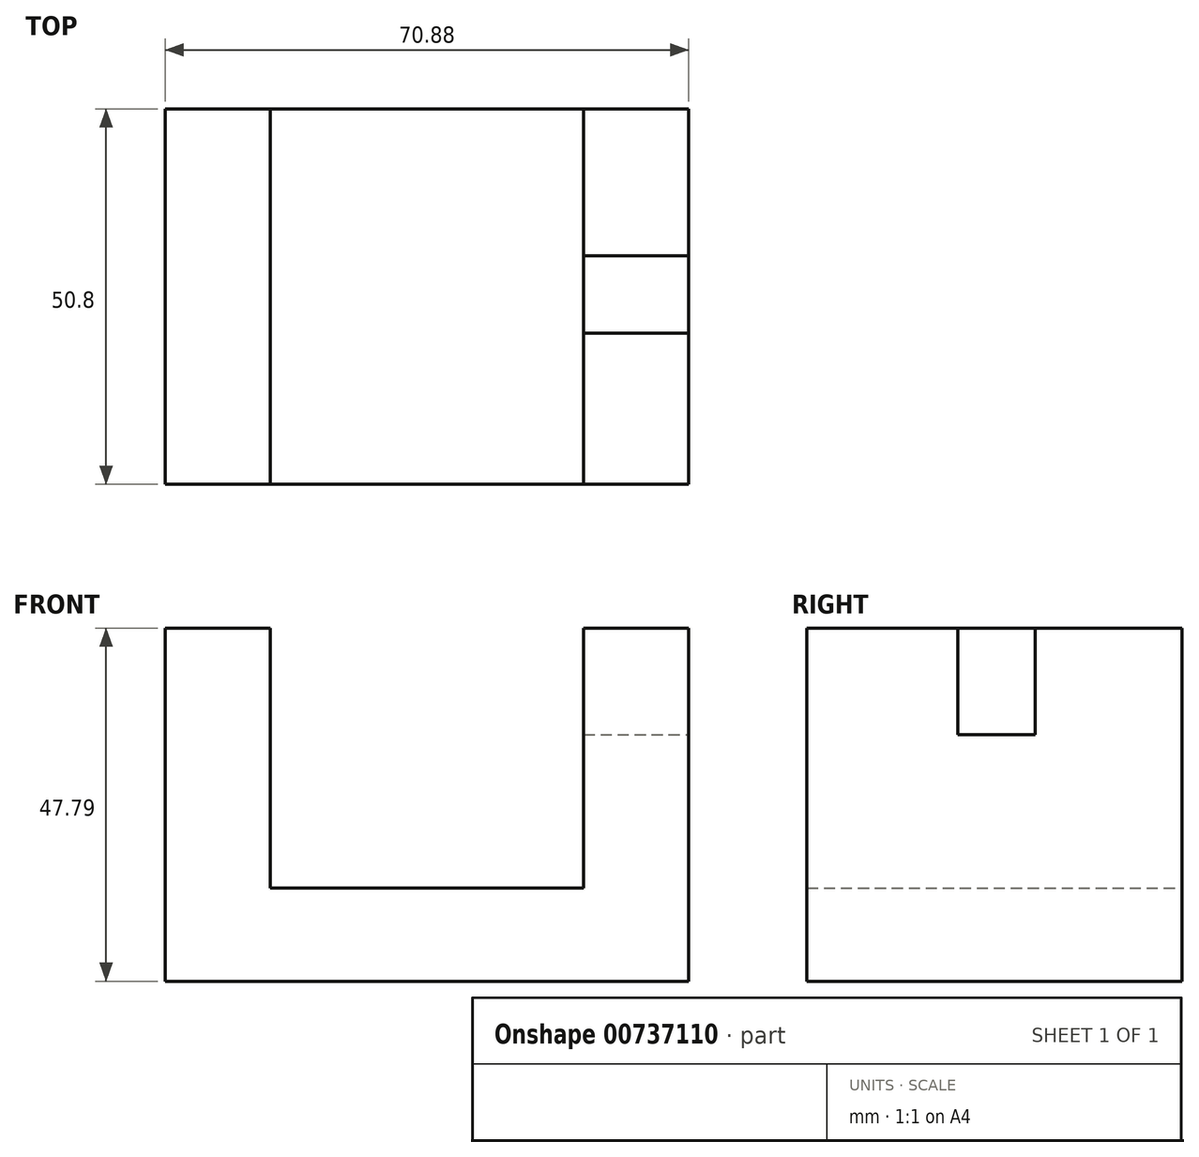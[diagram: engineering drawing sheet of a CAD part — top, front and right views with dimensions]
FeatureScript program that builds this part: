
annotation { "Feature Type Name" : "Feature", "Feature Type Description" : "" }
export const myFeature = defineFeature(function(context is Context, id is Id, definition is map)
    precondition{}
    {
        {
            var Q0;
            Q0=qCreatedBy(makeId("Front.planeOp"),FACE);
            var sketch = newSketch(context, id + "F0", { "sketchPlane" : qUnion([Q0])});
            skLineSegment(sketch, "E0.bottom", {"start": v(-36.38, -24.3) * mm, "end": v(34.5, -24.3) * mm});
            skLineSegment(sketch, "E0.top", {"start": v(-36.38, 23.5) * mm, "end": v(-22.15, 23.5) * mm});
            skLineSegment(sketch, "E0.left", {"start": v(-36.38, -24.3) * mm, "end": v(-36.38, 23.5) * mm});
            skLineSegment(sketch, "E0.right", {"start": v(34.5, -24.3) * mm, "end": v(34.5, 23.5) * mm});
            skLineSegment(sketch, "E1", {"start": v(-22.15, 23.5) * mm, "end": v(-22.15, -11.68) * mm});
            skLineSegment(sketch, "E2", {"start": v(-22.15, -11.68) * mm, "end": v(20.27, -11.68) * mm});
            skLineSegment(sketch, "E3", {"start": v(20.27, -11.68) * mm, "end": v(20.27, 23.5) * mm});
            skLineSegment(sketch, "E4.trimOffspring", {"start": v(20.27, 23.5) * mm, "end": v(34.5, 23.5) * mm});
            skSolve(sketch);
        }
        {
            var Q0;
            Q0 = qSketchRegion(id + "F0", true);
            extrude(context, id + "F1", {"entities" : qUnion([Q0]), "endBound" : BoundingType.SYMMETRIC, "depth" : 50.8 * mm, "offsetDistance" : 25.4 * mm});
        }
        {
            var Q0;
            Q0=makeQuery(id+"F1.opExtrude","SWEPT_FACE",FACE,{"disambiguationData":[OSD([sQuery(id+"F0.wireOp",EDGE,"E4.trimOffspring")])]});
            var sketch = newSketch(context, id + "F2", { "sketchPlane" : qUnion([Q0])});
            skLineSegment(sketch, "E5", {"start": v(20.27, 5.5) * mm, "end": v(34.5, 5.5) * mm});
            skLineSegment(sketch, "E6", {"start": v(20.27, -4.97) * mm, "end": v(34.5, -4.97) * mm});
            skSolve(sketch);
        }
        {
            var Q0;
            {var subQ0=sQuery(id+"F2.wireOp",EDGE,"E5");Q0=makeQuery(id+"F2.imprint","IMPRINT",FACE,{"disambiguationData":[TD([[makeQuery(id+"F2.imprint","IMPRINT",EDGE,{"derivedFrom":subQ0}),-1.0]])]});}
            extrude(context, id + "F3", {"entities" : qUnion([Q0]), "operationType" : NewBodyOperationType.REMOVE, "oppositeDirection" : true, "depth" : 14.42 * mm, "offsetDistance" : 25.4 * mm});
        }
    });
